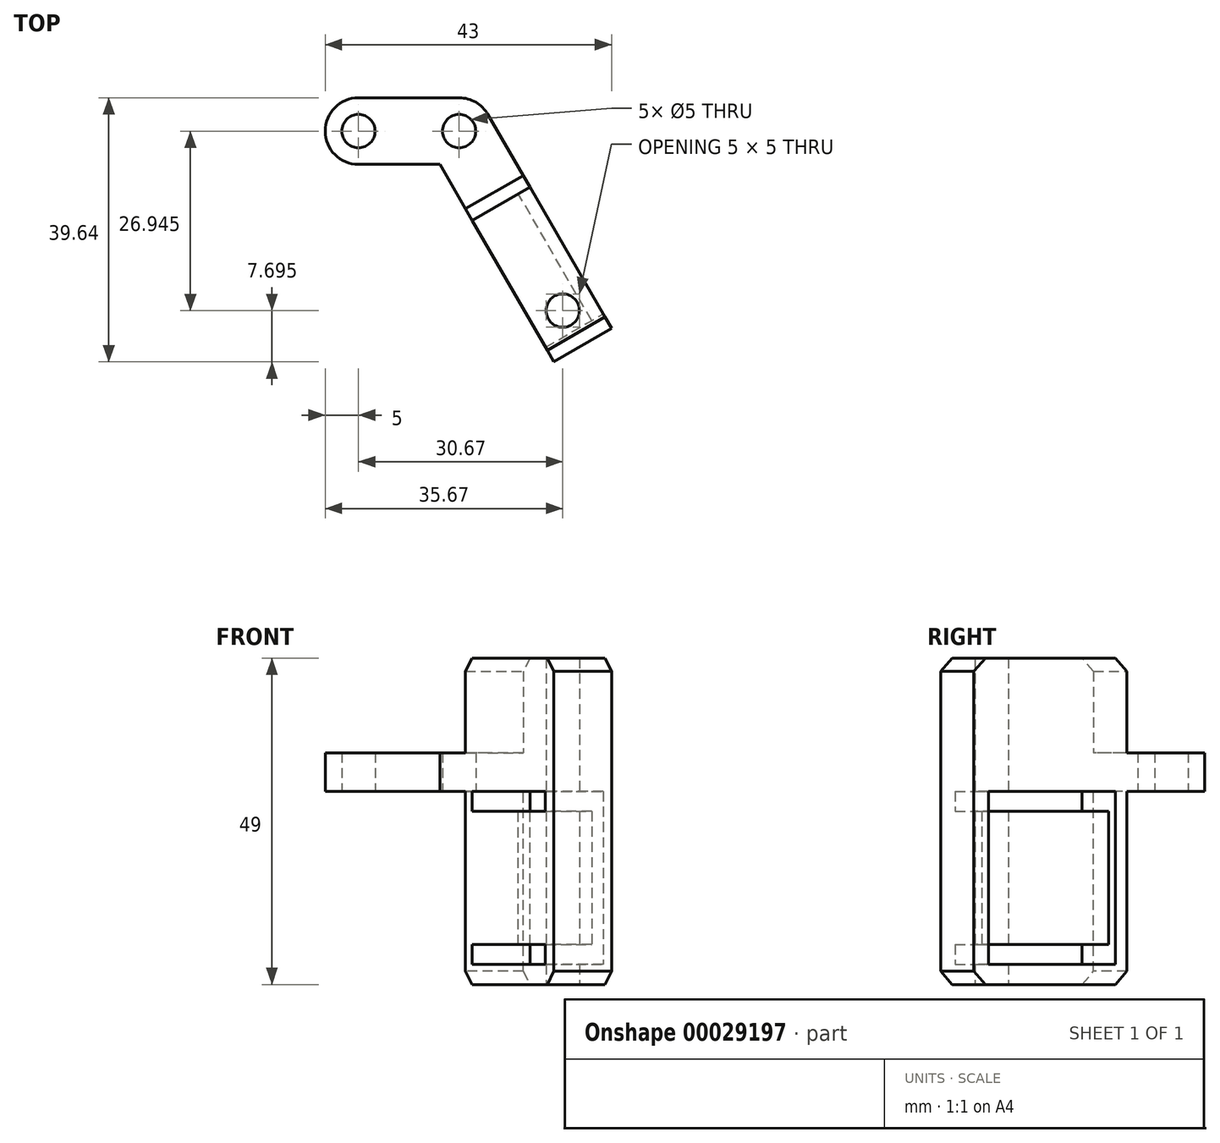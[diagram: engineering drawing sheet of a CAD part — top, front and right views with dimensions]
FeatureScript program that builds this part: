
annotation { "Feature Type Name" : "Feature", "Feature Type Description" : "" }
export const myFeature = defineFeature(function(context is Context, id is Id, definition is map)
    precondition{}
    {
        {
            var Q0;
            Q0=qCreatedBy(makeId("Top.planeOp"),FACE);
            var sketch = newSketch(context, id + "F0", { "sketchPlane" : qUnion([Q0])});
            skLineSegment(sketch, "E0", {"start": v(5, 0) * mm, "end": v(20.11, 0) * mm});
            skLineSegment(sketch, "E1", {"start": v(24.44, 2.5) * mm, "end": v(43, 34.64) * mm});
            skLineSegment(sketch, "E2", {"start": v(43, 34.64) * mm, "end": v(34.34, 39.64) * mm});
            skLineSegment(sketch, "E3", {"start": v(0, 5) * mm, "end": v(0, 5) * mm});
            skLineSegment(sketch, "E4", {"start": v(5, 10) * mm, "end": v(17.23, 10) * mm});
            skLineSegment(sketch, "E5", {"start": v(17.23, 10) * mm, "end": v(34.34, 39.64) * mm});
            skCircle(sketch, "E6", {"center": v(5, 5) * mm, "radius": 2.5 * mm});
            skCircle(sketch, "E7", {"center": v(35.67, 31.94) * mm, "radius": 2.5 * mm});
            skPoint(sketch, "E8.visualSharp", {"position": v(0, 10) * mm});
            skArc(sketch, "E8.filletArc", {"start": v(5, 10) * mm, "mid": v(1.46, 8.54) * mm, "end": v(0, 5) * mm});
            skPoint(sketch, "E9.visualSharp", {"position": v(0, 0) * mm});
            skArc(sketch, "E9.filletArc", {"start": v(0, 5) * mm, "mid": v(1.46, 1.46) * mm, "end": v(5, 0) * mm});
            skPoint(sketch, "E10.visualSharp", {"position": v(23, 0) * mm});
            skArc(sketch, "E10.filletArc", {"start": v(20.11, 0) * mm, "mid": v(22.61, 0.67) * mm, "end": v(24.44, 2.5) * mm});
            skCircle(sketch, "E11", {"center": v(20.11, 5) * mm, "radius": 2.5 * mm});
            skLineSegment(sketch, "E12", {"start": v(21.08, 16.67) * mm, "end": v(29.74, 11.67) * mm});
            skLineSegment(sketch, "E13", {"start": v(-47.49, 5) * mm, "end": v(66.25, 5) * mm, "construction": true});
            skArc(sketch, "E14.MirrorCS", {"start": v(20.11, 10) * mm, "mid": v(22.61, 9.33) * mm, "end": v(24.44, 7.5) * mm});
            skPoint(sketch, "E15.MirrorP", {"position": v(23, 10) * mm});
            skLineSegment(sketch, "E16.MirrorCS", {"start": v(24.44, 7.5) * mm, "end": v(43, -24.64) * mm});
            skLineSegment(sketch, "E17.MirrorCS", {"start": v(43, -24.64) * mm, "end": v(34.34, -29.64) * mm});
            skLineSegment(sketch, "E18.MirrorCS", {"start": v(5, 0) * mm, "end": v(17.23, 0) * mm});
            skLineSegment(sketch, "E19.MirrorCS", {"start": v(17.23, 0) * mm, "end": v(34.34, -29.64) * mm});
            skCircle(sketch, "E20.MirrorC", {"center": v(35.67, -21.94) * mm, "radius": 2.5 * mm});
            skLineSegment(sketch, "E21.MirrorCS", {"start": v(21.08, -6.67) * mm, "end": v(29.74, -1.67) * mm});
            skLineSegment(sketch, "E22.MirrorCS", {"start": v(5, 10) * mm, "end": v(20.11, 10) * mm});
            skSolve(sketch);
        }
        {
            var Q0;
            Q0=makeQuery(id+"F0.imprint","IMPRINT",FACE,{"disambiguationData":[TD([[makeQuery(id+"F0.imprint","IMPRINT",EDGE,{"derivedFrom":sQuery(id+"F0.wireOp",EDGE,"E0")}),1.0]])]});
            var Q1;
            {var subQ2=sQuery(id+"F0.wireOp",EDGE,"E0");Q1=makeQuery(id+"F0.imprint","IMPRINT",FACE,{"disambiguationData":[TD([[makeQuery(id+"F0.imprint","IMPRINT",EDGE,{"derivedFrom":subQ2}),-1.0]])]});}
            var Q2;
            {var subQ2=sQuery(id+"F0.wireOp",EDGE,"E17.MirrorCS");Q2=makeQuery(id+"F0.imprint","IMPRINT",FACE,{"disambiguationData":[TD([[makeQuery(id+"F0.imprint","IMPRINT",EDGE,{"derivedFrom":subQ2}),-1.0]])]});}
            extrude(context, id + "F1", {"entities" : qUnion([Q0, Q1, Q2]), "depth" : 5.8 * mm});
        }
        {
            var Q0;
            {var subQ2=sQuery(id+"F0.wireOp",EDGE,"E17.MirrorCS");Q0=makeQuery(id+"F0.imprint","IMPRINT",FACE,{"disambiguationData":[TD([[makeQuery(id+"F0.imprint","IMPRINT",EDGE,{"derivedFrom":subQ2}),-1.0]])]});}
            extrude(context, id + "F2", {"entities" : qUnion([Q0]), "operationType" : NewBodyOperationType.ADD, "depth" : 20 * mm});
        }
        {
            var Q0;
            {var subQ2=sQuery(id+"F0.wireOp",EDGE,"E17.MirrorCS");Q0=makeQuery(id+"F0.imprint","IMPRINT",FACE,{"disambiguationData":[TD([[makeQuery(id+"F0.imprint","IMPRINT",EDGE,{"derivedFrom":subQ2}),-1.0]])]});}
            extrude(context, id + "F3", {"entities" : qUnion([Q0]), "operationType" : NewBodyOperationType.ADD, "oppositeDirection" : true, "depth" : 29 * mm});
        }
        {
            var Q0;
            Q0=makeQuery(id+"F2.opExtrude","CAP_EDGE",EDGE,{"disambiguationData":[OSD([sQuery(id+"F0.wireOp",EDGE,"E21.MirrorCS")])],"isStart":false});
            var Q1;
            Q1=makeQuery(id+"F2.opExtrude","CAP_EDGE",EDGE,{"disambiguationData":[OSD([sQuery(id+"F0.wireOp",EDGE,"E17.MirrorCS")])],"isStart":false});
            var Q2;
            Q2=makeQuery(id+"F3.opExtrude","CAP_EDGE",EDGE,{"disambiguationData":[OSD([sQuery(id+"F0.wireOp",EDGE,"E21.MirrorCS")])],"isStart":false});
            var Q3;
            Q3=makeQuery(id+"F3.opExtrude","CAP_EDGE",EDGE,{"disambiguationData":[OSD([sQuery(id+"F0.wireOp",EDGE,"E17.MirrorCS")])],"isStart":false});
            chamfer(context, id + "F4", {"entities" : qUnion([Q0, Q1, Q2, Q3]), "width" : 2 * mm, "tangentPropagation" : true});
        }
        {
            var Q0;
            {var subQ0=sQuery(id+"F0.wireOp",EDGE,"E16.MirrorCS");Q0=makeQuery(id+"F3.boolean.opBoolean","MERGE",FACE,{"derivedFrom":[makeQuery(id+"F2.boolean.opBoolean","MERGE",FACE,{"derivedFrom":[makeQuery(id+"F1.opExtrude","SWEPT_FACE",FACE,{"disambiguationData":[OSD([subQ0])]}),makeQuery(id+"F2.opExtrude","SWEPT_FACE",FACE,{"disambiguationData":[OSD([subQ0])]})]}),makeQuery(id+"F3.opExtrude","SWEPT_FACE",FACE,{"disambiguationData":[OSD([subQ0])]})]});}
            var sketch = newSketch(context, id + "F5", { "sketchPlane" : qUnion([Q0])});
            skLineSegment(sketch, "E23.bottom", {"start": v(-40.31, 0) * mm, "end": v(-18.31, 0) * mm});
            skLineSegment(sketch, "E23.top", {"start": v(-40.31, -3) * mm, "end": v(-18.31, -3) * mm});
            skLineSegment(sketch, "E23.left", {"start": v(-40.31, 0) * mm, "end": v(-40.31, -3) * mm});
            skLineSegment(sketch, "E23.right", {"start": v(-18.31, 0) * mm, "end": v(-18.31, -3) * mm});
            skPoint(sketch, "E24.firstSnap0", {"position": v(-40.31, -1.5) * mm});
            skLineSegment(sketch, "E24.bottom", {"start": v(-40.31, -23) * mm, "end": v(-18.31, -23) * mm});
            skLineSegment(sketch, "E24.top", {"start": v(-40.31, -26) * mm, "end": v(-18.31, -26) * mm});
            skLineSegment(sketch, "E24.left", {"start": v(-40.31, -23) * mm, "end": v(-40.31, -26) * mm});
            skLineSegment(sketch, "E24.right", {"start": v(-18.31, -23) * mm, "end": v(-18.31, -26) * mm});
            skLineSegment(sketch, "E25", {"start": v(-40.31, -3) * mm, "end": v(-40.31, -23) * mm});
            skLineSegment(sketch, "E26", {"start": v(-18.31, -23) * mm, "end": v(-18.31, -3) * mm});
            skSolve(sketch);
        }
        {
            var Q0;
            Q0=makeQuery(id+"F5.imprint","IMPRINT",FACE,{"disambiguationData":[TD([[makeQuery(id+"F5.imprint","IMPRINT",EDGE,{"derivedFrom":sQuery(id+"F5.wireOp",EDGE,"E23.top")}),-1.0]])]});
            extrude(context, id + "F6", {"entities" : qUnion([Q0]), "operationType" : NewBodyOperationType.REMOVE, "oppositeDirection" : true, "depth" : 2 * mm});
        }
        {
            var Q0;
            Q0=makeQuery(id+"F5.imprint","IMPRINT",FACE,{"disambiguationData":[TD([[makeQuery(id+"F5.imprint","IMPRINT",EDGE,{"derivedFrom":sQuery(id+"F5.wireOp",EDGE,"E24.bottom")}),-1.0]])]});
            var Q1;
            Q1=makeQuery(id+"F5.imprint","IMPRINT",FACE,{"disambiguationData":[TD([[makeQuery(id+"F5.imprint","IMPRINT",EDGE,{"derivedFrom":sQuery(id+"F5.wireOp",EDGE,"E23.bottom")}),-1.0]])]});
            extrude(context, id + "F7", {"entities" : qUnion([Q0, Q1]), "operationType" : NewBodyOperationType.REMOVE, "endBound" : BoundingType.THROUGH_ALL, "oppositeDirection" : true, "depth" : 25 * mm});
        }
    });
